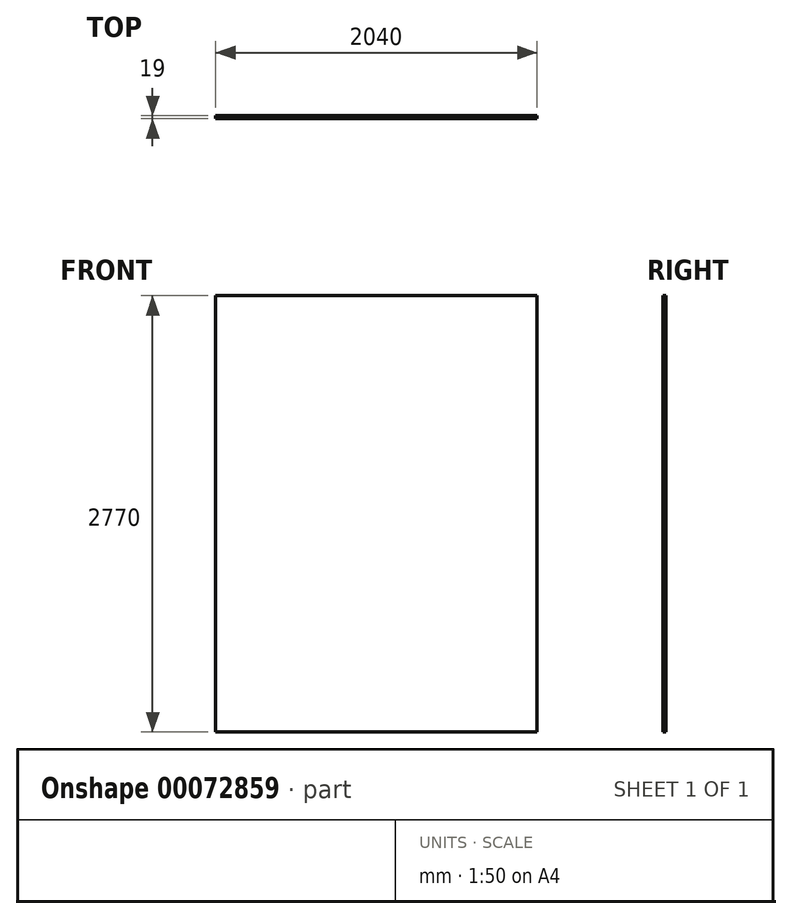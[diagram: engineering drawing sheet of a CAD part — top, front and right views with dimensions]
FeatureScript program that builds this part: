
annotation { "Feature Type Name" : "Feature", "Feature Type Description" : "" }
export const myFeature = defineFeature(function(context is Context, id is Id, definition is map)
    precondition{}
    {
        {
            var Q0;
            Q0=qCreatedBy(makeId("Front.planeOp"),FACE);
            var sketch = newSketch(context, id + "F0", { "sketchPlane" : qUnion([Q0])});
            skLineSegment(sketch, "E0.bottom", {"start": v(0, 0) * mm, "end": v(2040, 0) * mm});
            skLineSegment(sketch, "E0.top", {"start": v(0, -2770) * mm, "end": v(2040, -2770) * mm});
            skLineSegment(sketch, "E0.left", {"start": v(0, 0) * mm, "end": v(0, -2770) * mm});
            skLineSegment(sketch, "E0.right", {"start": v(2040, 0) * mm, "end": v(2040, -2770) * mm});
            skSolve(sketch);
        }
        {
            var Q0;
            Q0=makeQuery(id+"F0.imprint","IMPRINT",FACE,{"disambiguationData":[TD([[makeQuery(id+"F0.imprint","IMPRINT",EDGE,{"derivedFrom":sQuery(id+"F0.wireOp",EDGE,"E0.bottom")}),-1.0]])]});
            extrude(context, id + "F1", {"entities" : qUnion([Q0]), "depth" : 19 * mm});
        }
    });
